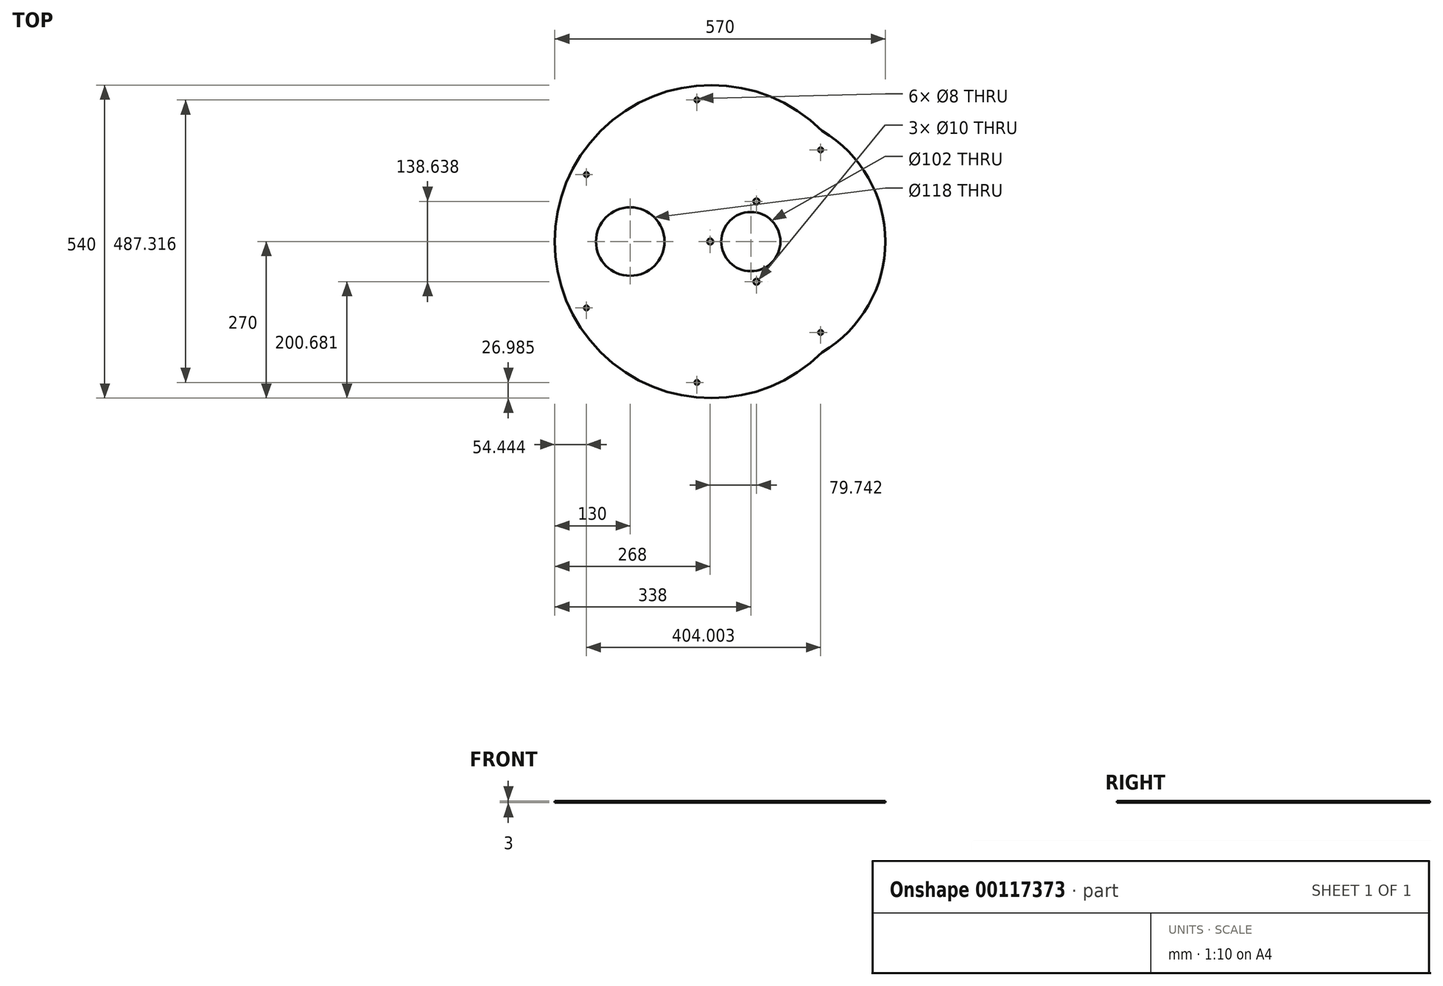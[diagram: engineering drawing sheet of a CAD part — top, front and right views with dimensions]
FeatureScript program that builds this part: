
annotation { "Feature Type Name" : "Feature", "Feature Type Description" : "" }
export const myFeature = defineFeature(function(context is Context, id is Id, definition is map)
    precondition{}
    {
        {
            var Q0;
            Q0=qCreatedBy(makeId("Top.planeOp"),FACE);
            var sketch = newSketch(context, id + "F0", { "sketchPlane" : qUnion([Q0])});
            skLineSegment(sketch, "E0", {"start": v(0, 0) * mm, "end": v(270, 0) * mm, "construction": true});
            skCircle(sketch, "E1", {"center": v(68, 0) * mm, "radius": 51 * mm});
            skCircle(sketch, "E2.0", {"center": v(68, 0) * mm, "radius": 70 * mm, "construction": true});
            skCircle(sketch, "E3", {"center": v(-2, 0) * mm, "radius": 5 * mm});
            skLineSegment(sketch, "E4", {"start": v(68, 0) * mm, "end": v(77.74, 69.32) * mm, "construction": true});
            skCircle(sketch, "E5", {"center": v(77.74, 69.32) * mm, "radius": 5 * mm});
            skCircle(sketch, "E6.MirrorC", {"center": v(77.74, -69.32) * mm, "radius": 5 * mm});
            skCircle(sketch, "E7.0", {"center": v(0, 0) * mm, "radius": 246 * mm, "construction": true});
            skLineSegment(sketch, "E8", {"start": v(0, 0) * mm, "end": v(206.83, 173.55) * mm, "construction": true});
            skLineSegment(sketch, "E9", {"start": v(270, 0) * mm, "end": v(300, 0) * mm, "construction": true});
            skArc(sketch, "E10", {"start": v(300, 0) * mm, "mid": v(270.8, 109.94) * mm, "end": v(190.92, 190.92) * mm});
            skLineSegment(sketch, "E11", {"start": v(0, 0) * mm, "end": v(190.92, 190.92) * mm, "construction": true});
            skArc(sketch, "E12.MirrorCS", {"start": v(300, 0) * mm, "mid": v(270.8, -109.94) * mm, "end": v(190.92, -190.92) * mm});
            skArc(sketch, "E13", {"start": v(190.92, 190.92) * mm, "mid": v(-270, 0) * mm, "end": v(190.92, -190.92) * mm});
            skArc(sketch, "E14", {"start": v(190.92, -190.92) * mm, "mid": v(270, 0) * mm, "end": v(190.92, 190.92) * mm, "construction": true});
            skCircle(sketch, "E15", {"center": v(-140, 0) * mm, "radius": 59 * mm});
            skLineSegment(sketch, "E16", {"start": v(0, 0) * mm, "end": v(-140, 0) * mm, "construction": true});
            skPoint(sketch, "E17", {"position": v(119, 0) * mm});
            skPoint(sketch, "E18", {"position": v(135, 0) * mm});
            skSolve(sketch);
        }
        {
            var Q0;
            Q0 = qSketchRegion(id + "F0", true);
            extrude(context, id + "F1", {"entities" : qUnion([Q0]), "depth" : 3 * mm});
        }
        {
            var Q0;
            Q0=makeQuery(id+"F1.opExtrude","CAP_FACE",FACE,{"disambiguationData":[OSD([sQuery(id+"F0.wireOp",EDGE,"E1"),sQuery(id+"F0.wireOp",EDGE,"E3"),sQuery(id+"F0.wireOp",EDGE,"E5"),sQuery(id+"F0.wireOp",EDGE,"E6.MirrorC"),sQuery(id+"F0.wireOp",EDGE,"E10"),sQuery(id+"F0.wireOp",EDGE,"E12.MirrorCS"),sQuery(id+"F0.wireOp",EDGE,"E13")])],"isStart":false});
            var sketch = newSketch(context, id + "F2", { "sketchPlane" : qUnion([Q0])});
            skCircle(sketch, "E19", {"center": v(188.45, 158.13) * mm, "radius": 4 * mm});
            skCircle(sketch, "E20.1.0", {"center": v(-24.84, 244.3) * mm, "radius": 4 * mm});
            skCircle(sketch, "E20.2.0", {"center": v(-215.56, 115.66) * mm, "radius": 4 * mm});
            skCircle(sketch, "E20.3.0", {"center": v(-215.56, -114.38) * mm, "radius": 4 * mm});
            skCircle(sketch, "E20.4.0", {"center": v(-24.84, -243.02) * mm, "radius": 4 * mm});
            skCircle(sketch, "E20.5.0", {"center": v(188.45, -156.84) * mm, "radius": 4 * mm});
            skPoint(sketch, "E20.center", {"position": v(0.77, 0.64) * mm});
            skLineSegment(sketch, "E20.anchor1", {"start": v(0.77, 0.64) * mm, "end": v(188.45, 158.13) * mm, "construction": true});
            skLineSegment(sketch, "E20.anchor2", {"start": v(0.77, 0.64) * mm, "end": v(188.45, -156.84) * mm, "construction": true});
            skSolve(sketch);
        }
        {
            var Q0;
            Q0 = qSketchRegion(id + "F2", true);
            extrude(context, id + "F3", {"entities" : qUnion([Q0]), "operationType" : NewBodyOperationType.REMOVE, "endBound" : BoundingType.THROUGH_ALL, "oppositeDirection" : true, "depth" : 25 * mm});
        }
    });
